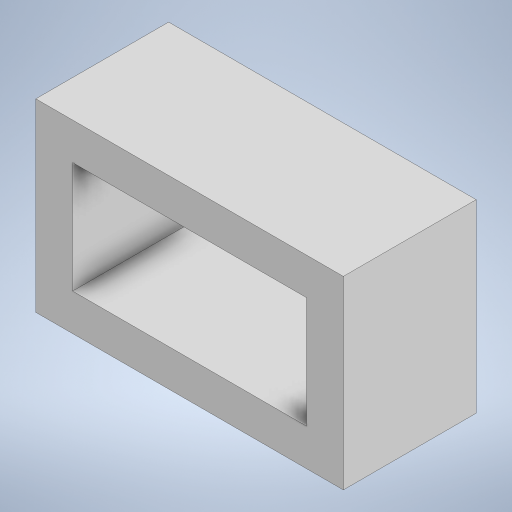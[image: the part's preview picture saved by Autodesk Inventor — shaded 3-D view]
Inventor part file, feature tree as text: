
AUTODESK INVENTOR PART (.ipt)
format: ipt  version: 2023 (Build 270158000, 158)  size: 560,640 bytes
history: native  units: mm
features: other x3, extrude x1, sketch x1
ambient origin geometry x8: Origin, YZ Plane, XZ Plane, XY Plane, X Axis, Y Axis, Z Axis, Center Point
bodies: Solid2 (feature_tree), Solid1 (feature_tree)
feature tree (5):
  other  "JST - XH - Thru (V) - 4Pin - 2.54mm.ipt"
  extrude  "Extrusion1"  Depth=0.1mm
  other  "Solid1::JST - XH - Thru (V) - 4Pin - 2.54mm.ipt"
  other  "TaggingFeature1"
  sketch  "Sketch1"  dims[d0=10.0mm d1=0.1mm d2=2.0mm d3=7.0mm d4=0.0mm]
